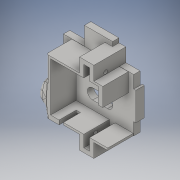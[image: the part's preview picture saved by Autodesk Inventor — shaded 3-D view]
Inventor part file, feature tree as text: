
AUTODESK INVENTOR PART (.ipt)
format: ipt  version: 2016 (Build 200138000, 138)  size: 539,136 bytes
history: native  units: in
note: dims shown in document units (in); Inventor stores cm internally (conversion verified against a paired STEP export)
features: sketch x15, other x3
ambient origin geometry x8: Origin, YZ Plane, XZ Plane, XY Plane, X Axis, Y Axis, Z Axis, Center Point
bodies: Solid1 (feature_tree)
feature tree (18):
  other  "Hip_holder_v2.ipt"
  other  "Solid1::Hip_holder_v2.ipt"
  other  "TaggingFeature1"
  sketch  "Sketch1"  dims[d0=0.3937in]
  sketch  "Sketch12"
  sketch  "Sketch14"
  sketch  "Sketch17"
  sketch  "Sketch18"
  sketch  "Sketch21"
  sketch  "Sketch22"
  sketch  "Sketch23"
  sketch  "Sketch24"
  sketch  "Sketch25"
  sketch  "Sketch26"
  sketch  "Sketch27"
  sketch  "Sketch28"
  sketch  "Sketch29"
  sketch  "Sketch30"
